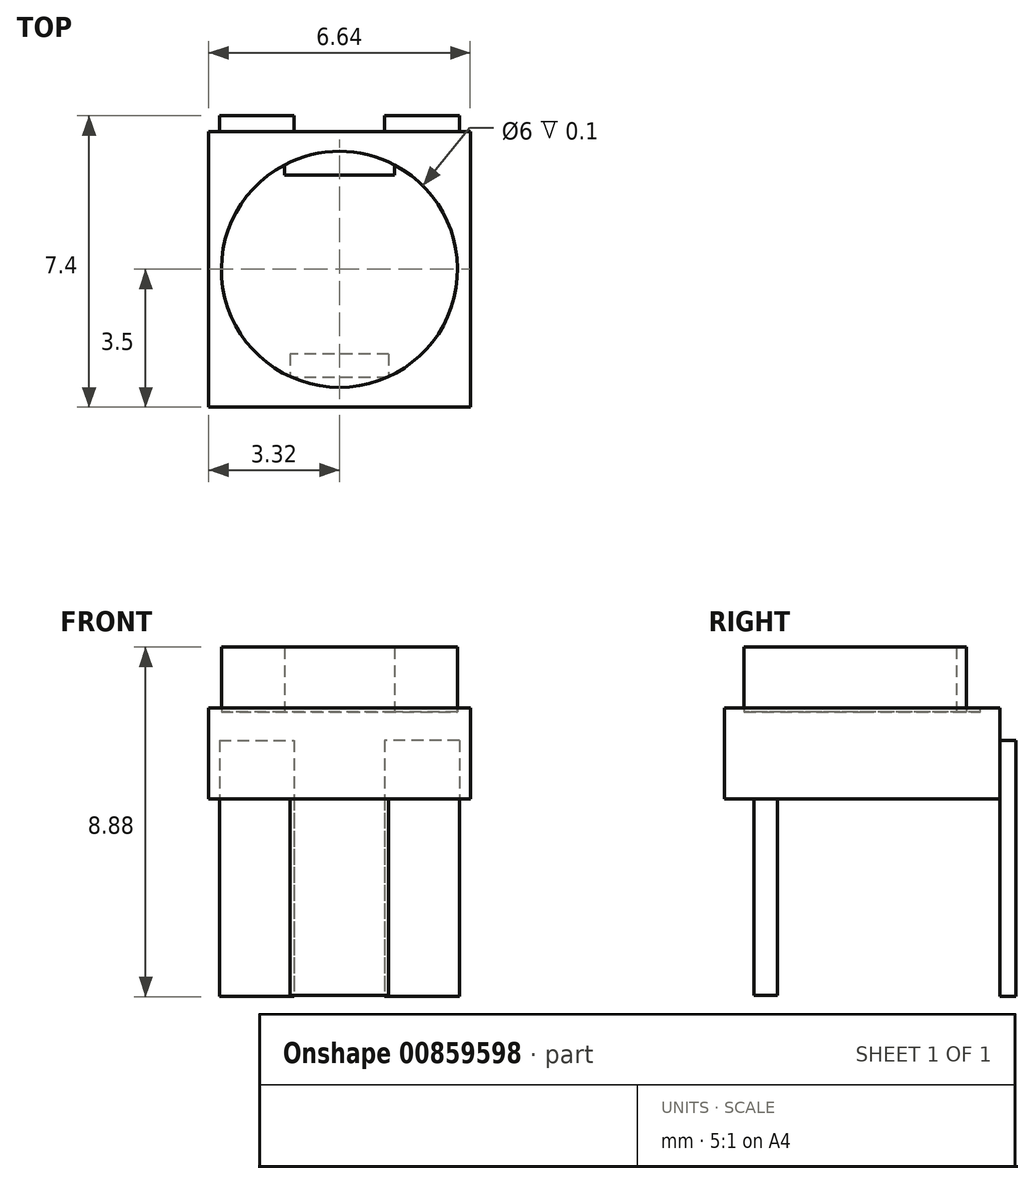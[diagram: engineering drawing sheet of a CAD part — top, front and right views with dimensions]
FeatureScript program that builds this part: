
annotation { "Feature Type Name" : "Feature", "Feature Type Description" : "" }
export const myFeature = defineFeature(function(context is Context, id is Id, definition is map)
    precondition{}
    {
        {
            var Q0;
            Q0=qCreatedBy(makeId("Top.planeOp"),FACE);
            var sketch = newSketch(context, id + "F0", { "sketchPlane" : qUnion([Q0])});
            skLineSegment(sketch, "E0.bottom", {"start": v(3.32, -3.5) * mm, "end": v(-3.33, -3.5) * mm});
            skLineSegment(sketch, "E0.top", {"start": v(3.33, 3.5) * mm, "end": v(-3.32, 3.5) * mm});
            skLineSegment(sketch, "E0.left", {"start": v(3.32, -3.5) * mm, "end": v(3.33, 3.5) * mm});
            skLineSegment(sketch, "E0.right", {"start": v(-3.33, -3.5) * mm, "end": v(-3.33, 3.5) * mm});
            skPoint(sketch, "E0.middle", {"position": v(0, 0) * mm});
            skSolve(sketch);
        }
        {
            var Q0;
            Q0 = qSketchRegion(id + "F0", true);
            extrude(context, id + "F1", {"entities" : qUnion([Q0]), "depth" : 2.3 * mm, "offsetDistance" : 25 * mm});
        }
        {
            var Q0;
            Q0=makeQuery(id+"F1.opExtrude","CAP_FACE",FACE,{"disambiguationData":[OSD([sQuery(id+"F0.wireOp",EDGE,"E0.bottom"),sQuery(id+"F0.wireOp",EDGE,"E0.top"),sQuery(id+"F0.wireOp",EDGE,"E0.left"),sQuery(id+"F0.wireOp",EDGE,"E0.right")])],"isStart":false});
            var sketch = newSketch(context, id + "F2", { "sketchPlane" : qUnion([Q0])});
            skCircle(sketch, "E1", {"center": v(0, 0) * mm, "radius": 3 * mm});
            skPoint(sketch, "E2", {"position": v(0, 3.5) * mm});
            skSolve(sketch);
        }
        {
            var Q0;
            Q0 = qSketchRegion(id + "F2", true);
            extrude(context, id + "F3", {"entities" : qUnion([Q0]), "operationType" : NewBodyOperationType.REMOVE, "oppositeDirection" : true, "depth" : .1 * mm, "offsetDistance" : 25 * mm});
        }
        {
            var Q0;
            Q0=makeQuery(id+"F1.opExtrude","CAP_FACE",FACE,{"disambiguationData":[OSD([sQuery(id+"F0.wireOp",EDGE,"E0.bottom"),sQuery(id+"F0.wireOp",EDGE,"E0.top"),sQuery(id+"F0.wireOp",EDGE,"E0.left"),sQuery(id+"F0.wireOp",EDGE,"E0.right")])],"isStart":true});
            var sketch = newSketch(context, id + "F4", { "sketchPlane" : qUnion([Q0])});
            skLineSegment(sketch, "E3.bottom", {"start": v(1.25, 2.15) * mm, "end": v(-1.25, 2.15) * mm});
            skLineSegment(sketch, "E3.top", {"start": v(1.25, 2.75) * mm, "end": v(-1.25, 2.75) * mm});
            skLineSegment(sketch, "E3.left", {"start": v(1.25, 2.15) * mm, "end": v(1.25, 2.75) * mm});
            skLineSegment(sketch, "E3.right", {"start": v(-1.25, 2.15) * mm, "end": v(-1.25, 2.75) * mm});
            skPoint(sketch, "E3.middle", {"position": v(0, 2.45) * mm});
            skSolve(sketch);
        }
        {
            var Q0;
            Q0 = qSketchRegion(id + "F4", true);
            extrude(context, id + "F5", {"entities" : qUnion([Q0]), "operationType" : NewBodyOperationType.ADD, "depth" : 5 * mm, "offsetDistance" : 25 * mm});
        }
        {
            var Q0;
            Q0=makeQuery(id+"F1.opExtrude","SWEPT_FACE",FACE,{"disambiguationData":[OSD([sQuery(id+"F0.wireOp",EDGE,"E0.top")])]});
            var sketch = newSketch(context, id + "F6", { "sketchPlane" : qUnion([Q0])});
            skPoint(sketch, "E4.middle.positionSnap0", {"position": v(3.32, 1.15) * mm});
            skPoint(sketch, "E4.centerSnap0", {"position": v(3.32, 1.15) * mm});
            skLineSegment(sketch, "E5.bottom", {"start": v(3.05, 1.48) * mm, "end": v(1.15, 1.48) * mm});
            skLineSegment(sketch, "E5.top", {"start": v(3.05, -5.03) * mm, "end": v(1.15, -5.03) * mm});
            skLineSegment(sketch, "E5.left", {"start": v(3.05, 1.48) * mm, "end": v(3.05, -5.03) * mm});
            skLineSegment(sketch, "E5.right", {"start": v(1.15, 1.48) * mm, "end": v(1.15, -5.03) * mm});
            skPoint(sketch, "E6.MirrorP", {"position": v(-3.33, 1.15) * mm});
            skLineSegment(sketch, "E7.MirrorCS", {"start": v(-1.15, 1.48) * mm, "end": v(-1.15, -5.03) * mm});
            skLineSegment(sketch, "E8.MirrorCS", {"start": v(-3.05, 1.48) * mm, "end": v(-3.05, -5.03) * mm});
            skLineSegment(sketch, "E9.MirrorCS", {"start": v(-3.05, -5.03) * mm, "end": v(-1.15, -5.03) * mm});
            skLineSegment(sketch, "E10.MirrorCS", {"start": v(-3.05, 1.48) * mm, "end": v(-1.15, 1.48) * mm});
            skSolve(sketch);
        }
        {
            var Q0;
            Q0 = qSketchRegion(id + "F6", true);
            extrude(context, id + "F7", {"entities" : qUnion([Q0]), "operationType" : NewBodyOperationType.ADD, "depth" : .4 * mm, "offsetDistance" : 25 * mm});
        }
        {
            var Q0;
            Q0=makeQuery(id+"F3.boolean.opBoolean","COPY",FACE,{"derivedFrom":makeQuery(id+"F3.opExtrude","CAP_FACE",FACE,{"disambiguationData":[OSD([sQuery(id+"F2.wireOp",EDGE,"E1")])],"isStart":false})});
            var sketch = newSketch(context, id + "F8", { "sketchPlane" : qUnion([Q0])});
            skArc(sketch, "E11.0", {"start": v(-1.4, 2.65) * mm, "mid": v(0, -3) * mm, "end": v(1.4, 2.65) * mm});
            skLineSegment(sketch, "E12.bottom", {"start": v(1.4, 2.4) * mm, "end": v(-1.4, 2.4) * mm});
            skLineSegment(sketch, "E12.left", {"start": v(1.4, 2.4) * mm, "end": v(1.4, 2.65) * mm});
            skLineSegment(sketch, "E12.right", {"start": v(-1.4, 2.4) * mm, "end": v(-1.4, 2.65) * mm});
            skSolve(sketch);
        }
        {
            var Q0;
            Q0 = qSketchRegion(id + "F8", true);
            extrude(context, id + "F9", {"entities" : qUnion([Q0]), "depth" : 1.65 * mm, "offsetDistance" : 25 * mm});
        }
    });
